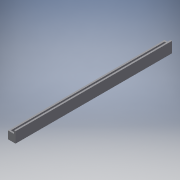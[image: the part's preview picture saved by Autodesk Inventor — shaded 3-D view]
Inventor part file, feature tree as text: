
AUTODESK INVENTOR PART (.ipt)
format: ipt  version: 2019.4 (Build 234330000, 330)  size: 120,832 bytes
history: native  units: mm
features: extrude x3, sketch x3, other x1
ambient origin geometry x8: Origin, YZ Plane, XZ Plane, XY Plane, X Axis, Y Axis, Z Axis, Center Point
bodies: Body1 (feature_tree)
feature tree (7):
  other  "Sólido1"
  extrude  "Extrusão1"  Depth=10.0mm
  extrude  "Extrusão2"  Depth=50.0mm
  extrude  "Extrusão3"  Depth=70.0mm
  sketch  "Esboço1"  dims[d0=10.0mm d1=10.0mm]
  sketch  "Esboço2"  dims[d2=10.0mm d3=50.0mm]
  sketch  "Esboço3"  dims[d4=50.0mm d5=70.0mm d6=1020.0mm d7=0.0mm d8=10.0mm d9=0.0mm d10=10.0mm d11=0.0mm]
